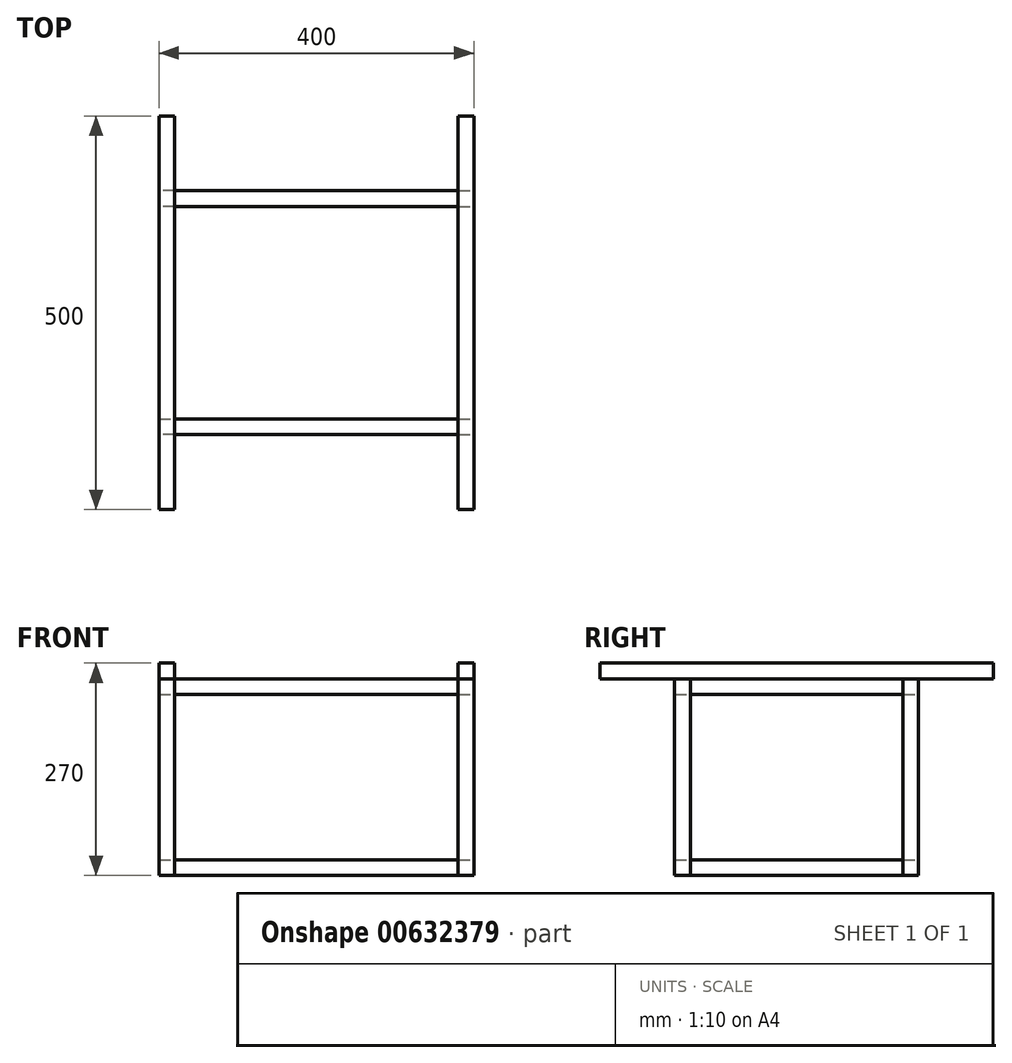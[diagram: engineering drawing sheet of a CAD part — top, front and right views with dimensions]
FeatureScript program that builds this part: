
annotation { "Feature Type Name" : "Feature", "Feature Type Description" : "" }
export const myFeature = defineFeature(function(context is Context, id is Id, definition is map)
    precondition{}
    {
        {
            var Q0;
            Q0=qCreatedBy(makeId("Front.planeOp"),FACE);
            var sketch = newSketch(context, id + "F0", { "sketchPlane" : qUnion([Q0])});
            skLineSegment(sketch, "E0.bottom", {"start": v(-180, 20) * mm, "end": v(-200, 20) * mm});
            skLineSegment(sketch, "E0.top", {"start": v(-180, 0) * mm, "end": v(-200, 0) * mm});
            skLineSegment(sketch, "E0.left", {"start": v(-180, 20) * mm, "end": v(-180, 0) * mm});
            skLineSegment(sketch, "E0.right", {"start": v(-200, 20) * mm, "end": v(-200, 0) * mm});
            skPoint(sketch, "E0.middle", {"position": v(-190, 10) * mm});
            skLineSegment(sketch, "E1.bottom", {"start": v(200, 20) * mm, "end": v(180, 20) * mm});
            skLineSegment(sketch, "E1.top", {"start": v(200, 0) * mm, "end": v(180, 0) * mm});
            skLineSegment(sketch, "E1.left", {"start": v(200, 20) * mm, "end": v(200, 0) * mm});
            skLineSegment(sketch, "E1.right", {"start": v(180, 20) * mm, "end": v(180, 0) * mm});
            skPoint(sketch, "E1.middle", {"position": v(190, 10) * mm});
            skLineSegment(sketch, "E2", {"start": v(0, 23.22) * mm, "end": v(0, -21.06) * mm, "construction": true});
            skSolve(sketch);
        }
        {
            var Q0;
            Q0 = qSketchRegion(id + "F0", true);
            extrude(context, id + "F1", {"entities" : qUnion([Q0]), "endBound" : BoundingType.SYMMETRIC, "depth" : 500 * mm, "offsetDistance" : 25 * mm});
        }
        {
            var Q0;
            Q0=makeQuery(id+"F1.opExtrude","SWEPT_FACE",FACE,{"disambiguationData":[OSD([sQuery(id+"F0.wireOp",EDGE,"E0.top")])]});
            var sketch = newSketch(context, id + "F2", { "sketchPlane" : qUnion([Q0])});
            skLineSegment(sketch, "E3", {"start": v(0, 57.88) * mm, "end": v(0, -106.34) * mm, "construction": true});
            skLineSegment(sketch, "E4", {"start": v(-97.48, 0) * mm, "end": v(122.4, 0) * mm, "construction": true});
            skLineSegment(sketch, "E5.bottom", {"start": v(-180, 155) * mm, "end": v(-200, 155) * mm});
            skLineSegment(sketch, "E5.top", {"start": v(-180, 135) * mm, "end": v(-200, 135) * mm});
            skLineSegment(sketch, "E5.left", {"start": v(-180, 155) * mm, "end": v(-180, 135) * mm});
            skLineSegment(sketch, "E5.right", {"start": v(-200, 155) * mm, "end": v(-200, 135) * mm});
            skLineSegment(sketch, "E6.MirrorCS", {"start": v(180, 135) * mm, "end": v(200, 135) * mm});
            skLineSegment(sketch, "E7.MirrorCS", {"start": v(180, 155) * mm, "end": v(180, 135) * mm});
            skLineSegment(sketch, "E8.MirrorCS", {"start": v(180, 155) * mm, "end": v(200, 155) * mm});
            skLineSegment(sketch, "E9.MirrorCS", {"start": v(200, 155) * mm, "end": v(200, 135) * mm});
            skLineSegment(sketch, "E10.MirrorCS", {"start": v(180, -155) * mm, "end": v(180, -135) * mm});
            skLineSegment(sketch, "E11.MirrorCS", {"start": v(180, -135) * mm, "end": v(200, -135) * mm});
            skLineSegment(sketch, "E12.MirrorCS", {"start": v(180, -155) * mm, "end": v(200, -155) * mm});
            skLineSegment(sketch, "E13.MirrorCS", {"start": v(200, -155) * mm, "end": v(200, -135) * mm});
            skLineSegment(sketch, "E14.MirrorCS", {"start": v(-200, -155) * mm, "end": v(-200, -135) * mm});
            skLineSegment(sketch, "E15.MirrorCS", {"start": v(-180, -155) * mm, "end": v(-180, -135) * mm});
            skLineSegment(sketch, "E16.MirrorCS", {"start": v(-180, -135) * mm, "end": v(-200, -135) * mm});
            skLineSegment(sketch, "E17.MirrorCS", {"start": v(-180, -155) * mm, "end": v(-200, -155) * mm});
            skSolve(sketch);
        }
        {
            var Q0;
            Q0 = qSketchRegion(id + "F2", true);
            extrude(context, id + "F3", {"entities" : qUnion([Q0]), "depth" : 250 * mm, "offsetDistance" : 25 * mm});
        }
        {
            var Q0;
            Q0=makeQuery(id+"F3.opExtrude","SWEPT_FACE",FACE,{"disambiguationData":[OSD([sQuery(id+"F2.wireOp",EDGE,"E16.MirrorCS")])]});
            var sketch = newSketch(context, id + "F4", { "sketchPlane" : qUnion([Q0])});
            skLineSegment(sketch, "E18.bottom", {"start": v(-180, 0) * mm, "end": v(-200, 0) * mm});
            skLineSegment(sketch, "E18.top", {"start": v(-180, -20) * mm, "end": v(-200, -20) * mm});
            skLineSegment(sketch, "E18.left", {"start": v(-180, 0) * mm, "end": v(-180, -20) * mm});
            skLineSegment(sketch, "E18.right", {"start": v(-200, 0) * mm, "end": v(-200, -20) * mm});
            skLineSegment(sketch, "E19.bottom", {"start": v(-180, -250) * mm, "end": v(-200, -250) * mm});
            skLineSegment(sketch, "E19.top", {"start": v(-180, -230) * mm, "end": v(-200, -230) * mm});
            skLineSegment(sketch, "E19.left", {"start": v(-180, -250) * mm, "end": v(-180, -230) * mm});
            skLineSegment(sketch, "E19.right", {"start": v(-200, -250) * mm, "end": v(-200, -230) * mm});
            skLineSegment(sketch, "E20.MirrorCS", {"start": v(180, 0) * mm, "end": v(200, 0) * mm});
            skLineSegment(sketch, "E21.MirrorCS", {"start": v(180, -20) * mm, "end": v(200, -20) * mm});
            skLineSegment(sketch, "E22.MirrorCS", {"start": v(180, 0) * mm, "end": v(180, -20) * mm});
            skLineSegment(sketch, "E23.MirrorCS", {"start": v(200, 0) * mm, "end": v(200, -20) * mm});
            skLineSegment(sketch, "E24.MirrorCS", {"start": v(200, -250) * mm, "end": v(200, -230) * mm});
            skLineSegment(sketch, "E25.MirrorCS", {"start": v(180, -250) * mm, "end": v(180, -230) * mm});
            skLineSegment(sketch, "E26.MirrorCS", {"start": v(180, -250) * mm, "end": v(200, -250) * mm});
            skLineSegment(sketch, "E27.MirrorCS", {"start": v(180, -230) * mm, "end": v(200, -230) * mm});
            skSolve(sketch);
        }
        {
            var Q0;
            Q0 = qSketchRegion(id + "F4", true);
            extrude(context, id + "F5", {"entities" : qUnion([Q0]), "endBound" : BoundingType.UP_TO_NEXT, "depth" : 25 * mm, "offsetDistance" : 25 * mm});
        }
        {
            var Q0;
            Q0=makeQuery(id+"F3.opExtrude","SWEPT_FACE",FACE,{"disambiguationData":[OSD([sQuery(id+"F2.wireOp",EDGE,"E15.MirrorCS")])]});
            var sketch = newSketch(context, id + "F6", { "sketchPlane" : qUnion([Q0])});
            skLineSegment(sketch, "E28.bottom", {"start": v(155, 0) * mm, "end": v(135, 0) * mm});
            skLineSegment(sketch, "E28.top", {"start": v(155, -20) * mm, "end": v(135, -20) * mm});
            skLineSegment(sketch, "E28.left", {"start": v(155, 0) * mm, "end": v(155, -20) * mm});
            skLineSegment(sketch, "E28.right", {"start": v(135, 0) * mm, "end": v(135, -20) * mm});
            skLineSegment(sketch, "E29.bottom", {"start": v(155, -250) * mm, "end": v(135, -250) * mm});
            skLineSegment(sketch, "E29.top", {"start": v(155, -230) * mm, "end": v(135, -230) * mm});
            skLineSegment(sketch, "E29.left", {"start": v(155, -250) * mm, "end": v(155, -230) * mm});
            skLineSegment(sketch, "E29.right", {"start": v(135, -250) * mm, "end": v(135, -230) * mm});
            skLineSegment(sketch, "E30.MirrorCS", {"start": v(-135, -250) * mm, "end": v(-135, -230) * mm});
            skLineSegment(sketch, "E31.MirrorCS", {"start": v(-155, -250) * mm, "end": v(-155, -230) * mm});
            skLineSegment(sketch, "E32.MirrorCS", {"start": v(-155, -250) * mm, "end": v(-135, -250) * mm});
            skLineSegment(sketch, "E33.MirrorCS", {"start": v(-155, -230) * mm, "end": v(-135, -230) * mm});
            skLineSegment(sketch, "E34.MirrorCS", {"start": v(-155, 0) * mm, "end": v(-135, 0) * mm});
            skLineSegment(sketch, "E35.MirrorCS", {"start": v(-155, -20) * mm, "end": v(-135, -20) * mm});
            skLineSegment(sketch, "E36.MirrorCS", {"start": v(-135, 0) * mm, "end": v(-135, -20) * mm});
            skLineSegment(sketch, "E37.MirrorCS", {"start": v(-155, 0) * mm, "end": v(-155, -20) * mm});
            skSolve(sketch);
        }
        {
            var Q0;
            Q0 = qSketchRegion(id + "F6", true);
            extrude(context, id + "F7", {"entities" : qUnion([Q0]), "endBound" : BoundingType.UP_TO_NEXT, "depth" : 25 * mm, "offsetDistance" : 25 * mm});
        }
    });
